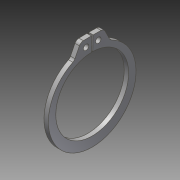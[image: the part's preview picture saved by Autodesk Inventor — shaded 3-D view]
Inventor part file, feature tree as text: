
AUTODESK INVENTOR PART (.ipt)
format: ipt  version: 2014 SP1 (Build 180222100, 222)  size: 98,304 bytes
history: native  units: in
note: dims shown in document units (in); Inventor stores cm internally (conversion verified against a paired STEP export)
features: fillet x1, other x1, imported_body x1
ambient origin geometry x8: Origin, YZ Plane, XZ Plane, XY Plane, X Axis, Y Axis, Z Axis, Center Point
bodies: Body1 (feature_tree)
feature tree (3):
  fillet  "Fillet1"  [1 undecoded]
  other  "217-2428-028 Rev1_97633A250.ipt1"
  imported_body  "Base1"
note: 1 required parameter value undecoded (feature->parameter linkage not recoverable at this tier; creation-order binding heuristic only, values carry confidence <= 0.55)
